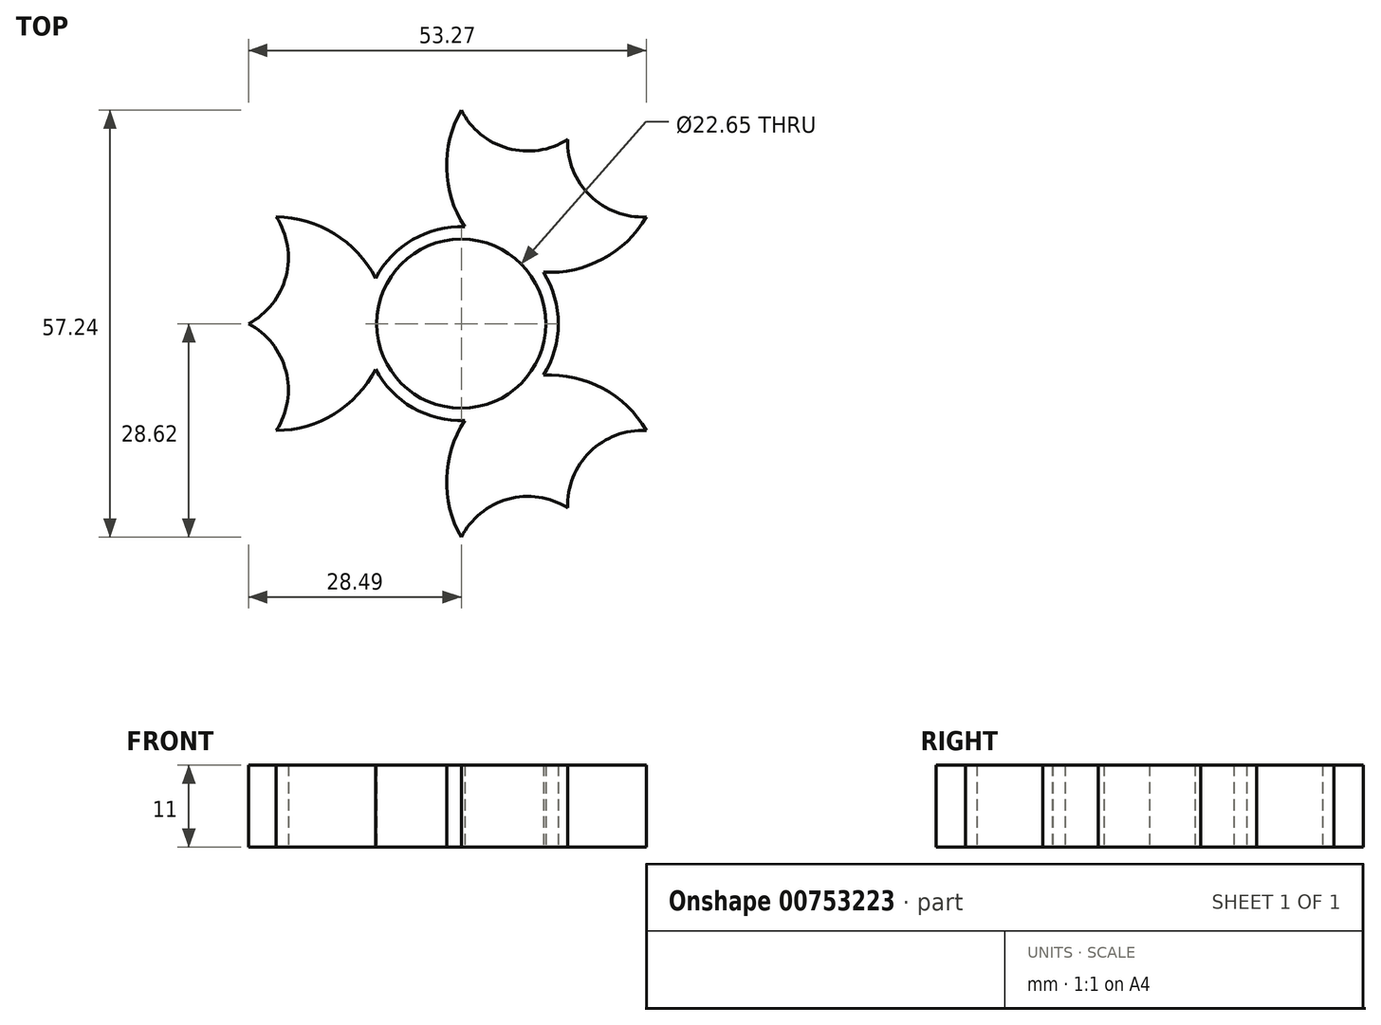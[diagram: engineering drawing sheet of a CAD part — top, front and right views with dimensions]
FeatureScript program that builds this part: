
annotation { "Feature Type Name" : "Feature", "Feature Type Description" : "" }
export const myFeature = defineFeature(function(context is Context, id is Id, definition is map)
    precondition{}
    {
        {
            var Q0;
            Q0=qCreatedBy(makeId("Top.planeOp"),FACE);
            var sketch = newSketch(context, id + "F0", { "sketchPlane" : qUnion([Q0])});
            skCircle(sketch, "E0", {"center": v(0, 0) * mm, "radius": 11.32 * mm});
            skCircle(sketch, "E1", {"center": v(0, 0) * mm, "radius": 13 * mm});
            skPoint(sketch, "E2.orphan", {"position": v(11.02, 6.9) * mm});
            skPoint(sketch, "E3.orphan", {"position": v(0.47, -13) * mm});
            skPoint(sketch, "E4.MirrorCS.start.orphan", {"position": v(4.53, 12.18) * mm});
            skPoint(sketch, "E5.start.orphan", {"position": v(-4.53, 12.18) * mm});
            skPoint(sketch, "E6.orphan", {"position": v(-12.82, -2.17) * mm});
            skPoint(sketch, "E7.orphan", {"position": v(-8.28, -10.02) * mm});
            skPoint(sketch, "E8.orphan", {"position": v(8.28, -10.02) * mm});
            skArc(sketch, "E9.1.0", {"start": v(-29.69, -0.54) * mm, "mid": v(-23.66, 5.7) * mm, "end": v(-24.78, 14.3) * mm});
            skArc(sketch, "E9.1.1", {"start": v(-11.49, 6.09) * mm, "mid": v(-16.98, 12.07) * mm, "end": v(-24.78, 14.3) * mm});
            skPoint(sketch, "E10.orphan", {"position": v(-29.69, -0.54) * mm});
            skPoint(sketch, "E11.orphan", {"position": v(15.3, -25.44) * mm});
            skArc(sketch, "E12.MirrorCS", {"start": v(-29.69, 0.54) * mm, "mid": v(-23.66, -5.7) * mm, "end": v(-24.78, -14.3) * mm});
            skArc(sketch, "E13.MirrorCS", {"start": v(-11.49, -6.09) * mm, "mid": v(-16.98, -12.07) * mm, "end": v(-24.78, -14.3) * mm});
            skArc(sketch, "E14.1.0", {"start": v(0.47, -13) * mm, "mid": v(-1.96, -20.74) * mm, "end": v(0, -28.62) * mm});
            skArc(sketch, "E14.1.1", {"start": v(15.3, -25.44) * mm, "mid": v(6.89, -23.35) * mm, "end": v(0, -28.62) * mm});
            skArc(sketch, "E14.1.2", {"start": v(14.38, -25.98) * mm, "mid": v(16.77, -17.64) * mm, "end": v(24.78, -14.3) * mm});
            skArc(sketch, "E14.1.3", {"start": v(11.02, -6.9) * mm, "mid": v(18.94, -8.67) * mm, "end": v(24.78, -14.3) * mm});
            skArc(sketch, "E14.2.0", {"start": v(11.02, 6.9) * mm, "mid": v(18.94, 8.67) * mm, "end": v(24.78, 14.3) * mm});
            skArc(sketch, "E14.2.1", {"start": v(14.38, 25.98) * mm, "mid": v(16.77, 17.64) * mm, "end": v(24.78, 14.3) * mm});
            skArc(sketch, "E14.2.2", {"start": v(15.3, 25.44) * mm, "mid": v(6.89, 23.35) * mm, "end": v(0, 28.62) * mm});
            skArc(sketch, "E14.2.3", {"start": v(0.47, 13) * mm, "mid": v(-1.96, 20.74) * mm, "end": v(0, 28.62) * mm});
            skSolve(sketch);
        }
        {
            var Q0;
            Q0 = qSketchRegion(id + "F0", true);
            extrude(context, id + "F1", {"entities" : qUnion([Q0]), "depth" : 11 * mm, "offsetDistance" : 25 * mm});
        }
    });
